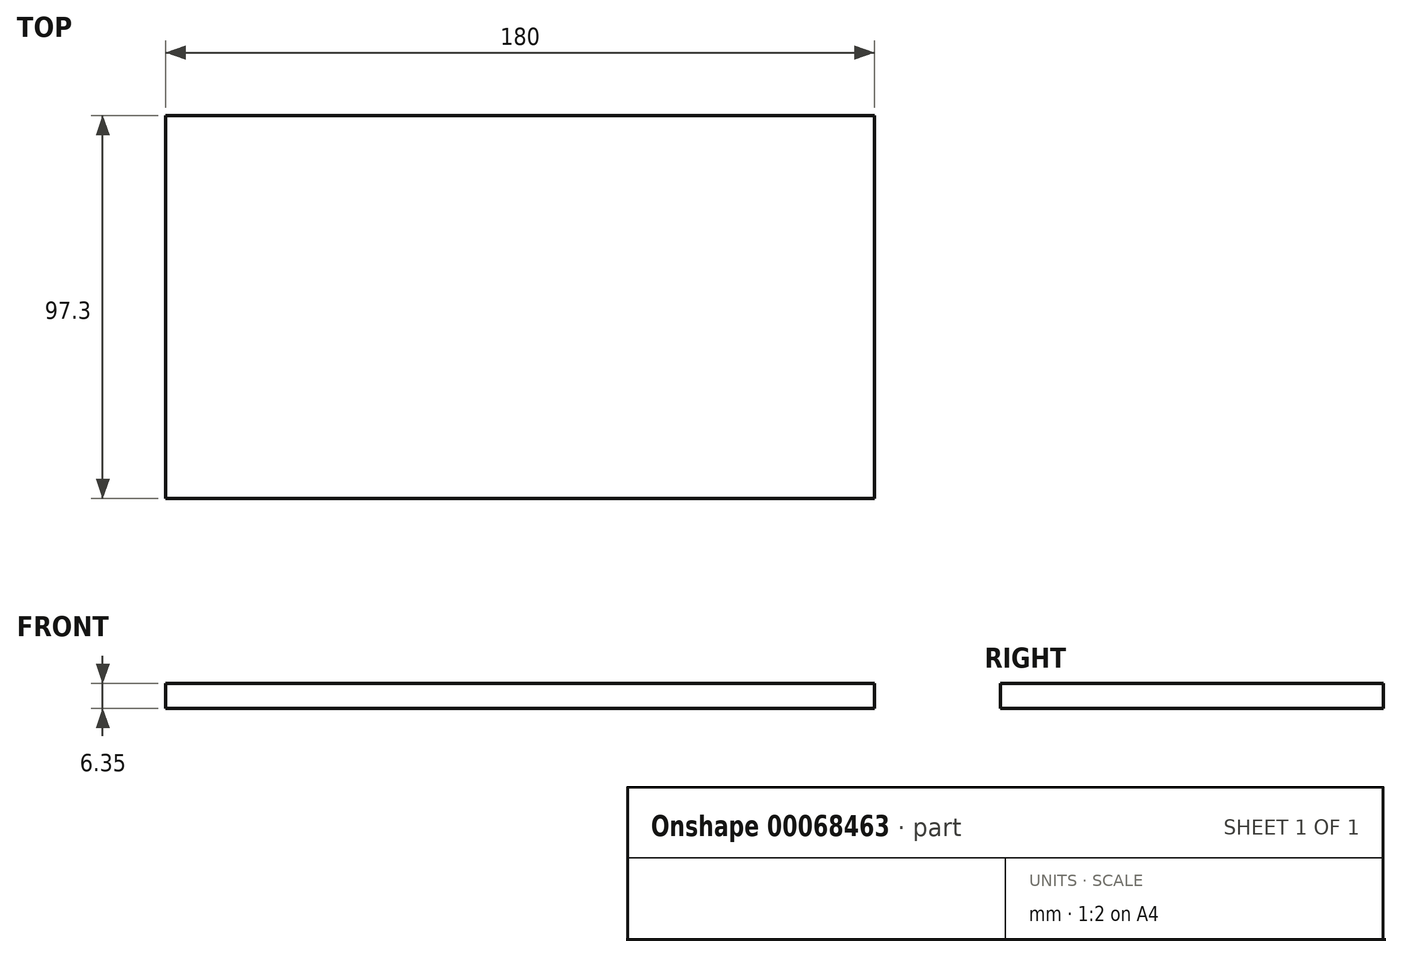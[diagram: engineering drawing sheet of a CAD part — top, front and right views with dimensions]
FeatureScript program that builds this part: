
annotation { "Feature Type Name" : "Feature", "Feature Type Description" : "" }
export const myFeature = defineFeature(function(context is Context, id is Id, definition is map)
    precondition{}
    {
        {
            var Q0;
            Q0=qCreatedBy(makeId("Top.planeOp"),FACE);
            var sketch = newSketch(context, id + "F0", { "sketchPlane" : qUnion([Q0])});
            skLineSegment(sketch, "E0.rect.bottom", {"start": v(90, 48.65) * mm, "end": v(-90, 48.65) * mm});
            skLineSegment(sketch, "E0.rect.top", {"start": v(90, -48.65) * mm, "end": v(-90, -48.65) * mm});
            skLineSegment(sketch, "E0.rect.left", {"start": v(90, 48.65) * mm, "end": v(90, -48.65) * mm});
            skLineSegment(sketch, "E0.rect.right", {"start": v(-90, 48.65) * mm, "end": v(-90, -48.65) * mm});
            skPoint(sketch, "E0.rect.middle", {"position": v(0, 0) * mm});
            skSolve(sketch);
        }
        {
            var Q0;
            Q0=makeQuery(id+"F0.imprint","IMPRINT",FACE,{"disambiguationData":[TD([[makeQuery(id+"F0.imprint","IMPRINT",EDGE,{"derivedFrom":sQuery(id+"F0.wireOp",EDGE,"E0.rect.bottom")}),1.0]])]});
            extrude(context, id + "F1", {"entities" : qUnion([Q0]), "depth" : 6.35 * mm});
        }
    });
